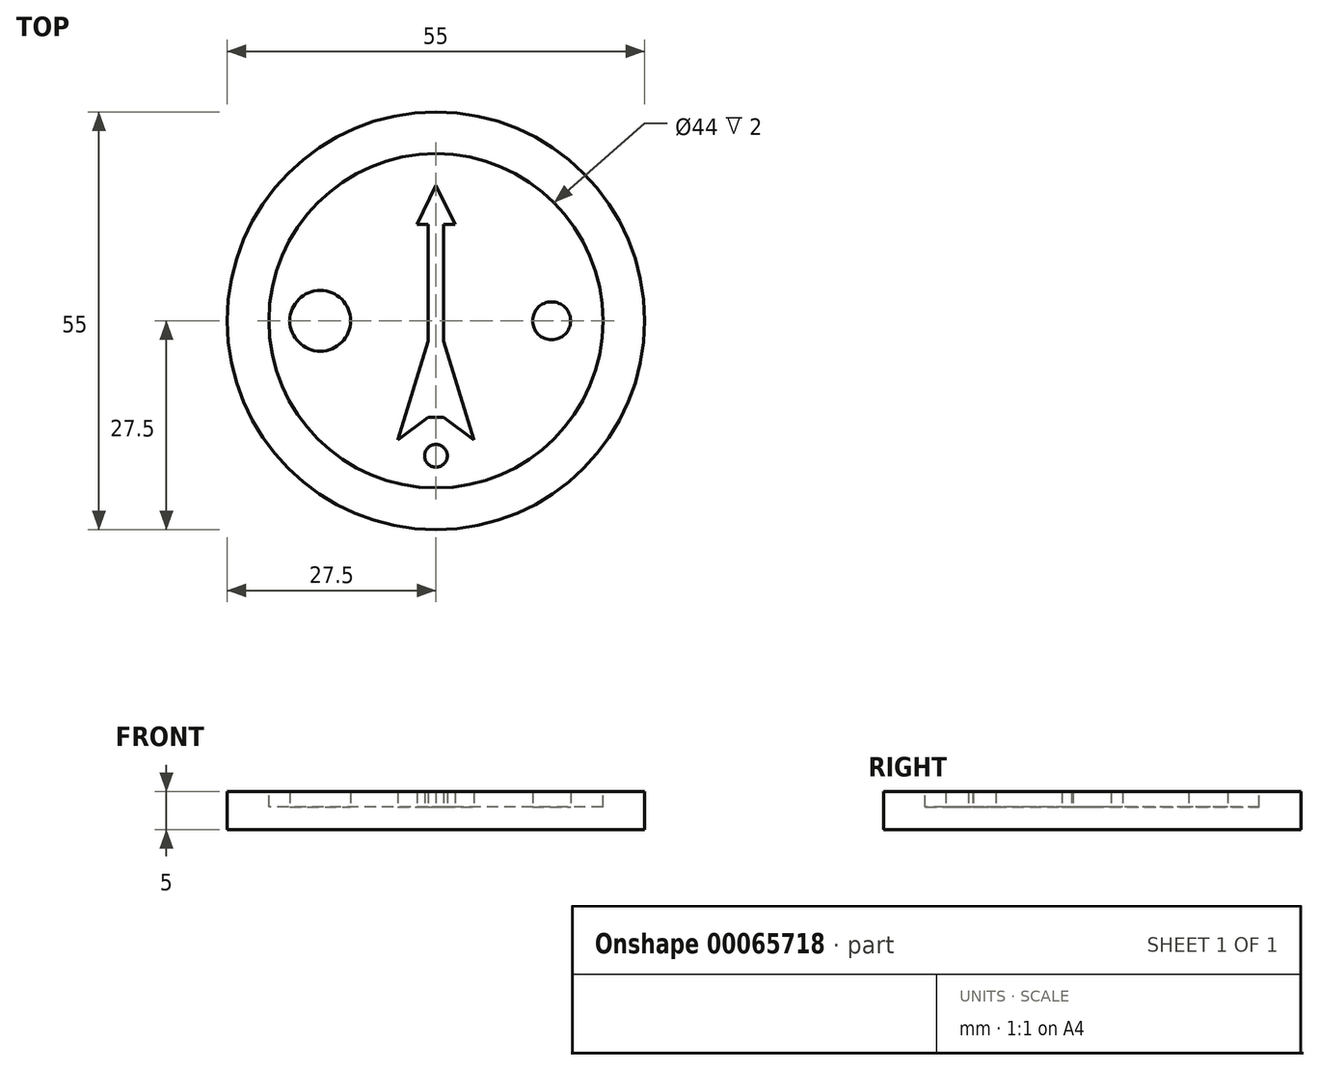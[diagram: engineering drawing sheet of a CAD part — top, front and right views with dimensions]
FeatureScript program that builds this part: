
annotation { "Feature Type Name" : "Feature", "Feature Type Description" : "" }
export const myFeature = defineFeature(function(context is Context, id is Id, definition is map)
    precondition{}
    {
        {
            var Q0;
            Q0=qCreatedBy(makeId("Front.planeOp"),FACE);
            var sketch = newSketch(context, id + "F0", { "sketchPlane" : qUnion([Q0])});
            skLineSegment(sketch, "E0", {"start": v(0, 0) * mm, "end": v(27.5, 0) * mm});
            skLineSegment(sketch, "E1", {"start": v(27.5, 0) * mm, "end": v(27.5, 5) * mm});
            skLineSegment(sketch, "E2", {"start": v(27.5, 5) * mm, "end": v(22, 5) * mm});
            skLineSegment(sketch, "E3", {"start": v(22, 5) * mm, "end": v(22, 3) * mm});
            skLineSegment(sketch, "E4", {"start": v(22, 3) * mm, "end": v(0, 3) * mm});
            skLineSegment(sketch, "E5", {"start": v(0, 3) * mm, "end": v(0, 0) * mm});
            skLineSegment(sketch, "E6", {"start": v(0, 43.2) * mm, "end": v(0, -38.3) * mm, "construction": true});
            skSolve(sketch);
        }
        {
            var Q0;
            Q0=makeQuery(id+"F0.imprint","IMPRINT",FACE,{"disambiguationData":[TD([[makeQuery(id+"F0.imprint","IMPRINT",EDGE,{"derivedFrom":sQuery(id+"F0.wireOp",EDGE,"E0")}),1.0]])]});
            var Q1;
            Q1=sQuery(id+"F0.wireOp",EDGE,"E6");
            revolve(context, id + "F1", {"entities" : qUnion([Q0]), "axis" : qUnion([Q1]), "revolveType" : RevolveType.FULL});
        }
        {
            var Q0;
            Q0=makeQuery(id+"F1.opRevolve","SWEPT_FACE",FACE,{"disambiguationData":[OSD([sQuery(id+"F0.wireOp",EDGE,"E4")])]});
            var sketch = newSketch(context, id + "F2", { "sketchPlane" : qUnion([Q0])});
            skLineSegment(sketch, "E7.rect.bottom", {"start": v(1, 12.7) * mm, "end": v(-1, 12.7) * mm});
            skLineSegment(sketch, "E7.rect.top", {"start": v(1, -12.7) * mm, "end": v(-1, -12.7) * mm});
            skLineSegment(sketch, "E7.rect.left", {"start": v(1, 12.7) * mm, "end": v(1, -12.7) * mm});
            skLineSegment(sketch, "E7.rect.right", {"start": v(-1, 12.7) * mm, "end": v(-1, -12.7) * mm});
            skPoint(sketch, "E7.rect.middle", {"position": v(0, 0) * mm});
            skLineSegment(sketch, "E8", {"start": v(-1, 12.7) * mm, "end": v(-2.5, 12.7) * mm});
            skLineSegment(sketch, "E9", {"start": v(-2.5, 12.7) * mm, "end": v(0, 17.86) * mm});
            skLineSegment(sketch, "E10", {"start": v(0, 17.86) * mm, "end": v(2.5, 12.7) * mm});
            skLineSegment(sketch, "E11", {"start": v(2.5, 12.7) * mm, "end": v(1, 12.7) * mm});
            skLineSegment(sketch, "E12", {"start": v(-2.5, 12.7) * mm, "end": v(9.08, 12.7) * mm, "construction": true});
            skLineSegment(sketch, "E13", {"start": v(-1, -2.7) * mm, "end": v(-5.01, -15.7) * mm});
            skLineSegment(sketch, "E14", {"start": v(-5.01, -15.7) * mm, "end": v(-1, -12.7) * mm});
            skLineSegment(sketch, "E15", {"start": v(1, -2.7) * mm, "end": v(5, -15.7) * mm});
            skLineSegment(sketch, "E16", {"start": v(5, -15.7) * mm, "end": v(1, -12.7) * mm});
            skLineSegment(sketch, "E17", {"start": v(1, -2.7) * mm, "end": v(-6.88, -2.7) * mm, "construction": true});
            skLineSegment(sketch, "E18", {"start": v(5, -15.7) * mm, "end": v(-9.76, -15.7) * mm, "construction": true});
            skCircle(sketch, "E19", {"center": v(-15.24, 0) * mm, "radius": 4 * mm});
            skCircle(sketch, "E20", {"center": v(15.24, 0) * mm, "radius": 2.5 * mm});
            skCircle(sketch, "E21", {"center": v(0, -17.78) * mm, "radius": 1.5 * mm});
            skSolve(sketch);
        }
        {
            var Q0;
            Q0 = qSketchRegion(id + "F2", true);
            var Q1;
            Q1=makeQuery(id+"F1.opRevolve","SWEPT_FACE",FACE,{"disambiguationData":[OSD([sQuery(id+"F0.wireOp",EDGE,"E2")])]});
            extrude(context, id + "F3", {"entities" : qUnion([Q0]), "operationType" : NewBodyOperationType.ADD, "endBound" : BoundingType.UP_TO_SURFACE, "endBoundEntityFace" : qUnion([Q1]), "depth" : 25.4 * mm});
        }
    });
